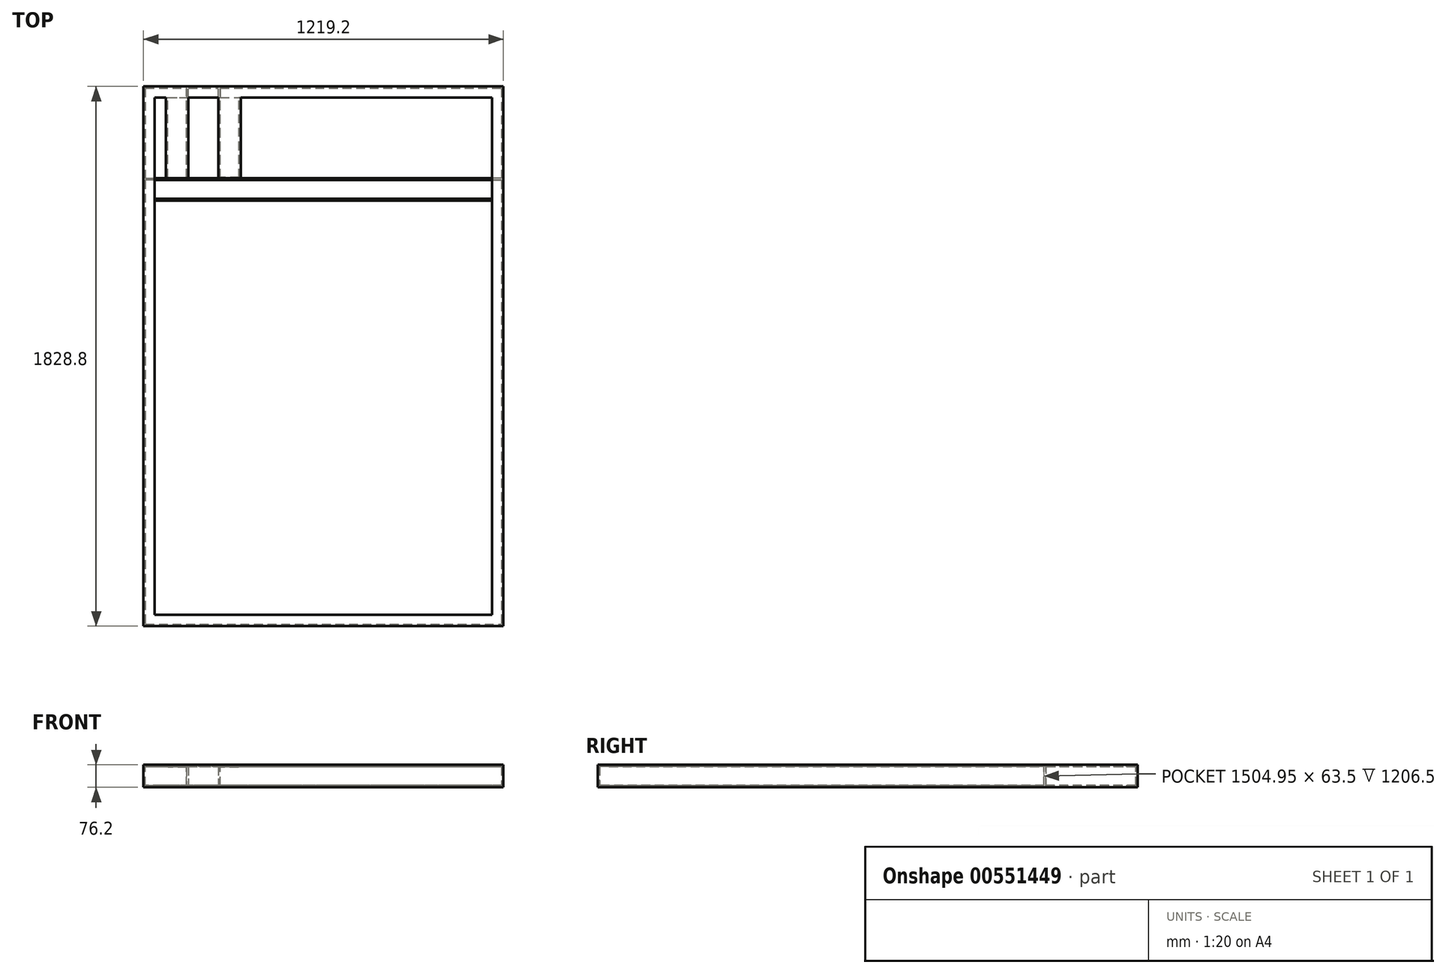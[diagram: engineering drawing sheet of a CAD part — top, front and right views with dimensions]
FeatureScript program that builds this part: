
annotation { "Feature Type Name" : "Feature", "Feature Type Description" : "" }
export const myFeature = defineFeature(function(context is Context, id is Id, definition is map)
    precondition{}
    {
        {
            var Q0;
            Q0=qCreatedBy(makeId("Top.planeOp"),FACE);
            var sketch = newSketch(context, id + "F0", { "sketchPlane" : qUnion([Q0])});
            skLineSegment(sketch, "E0.bottom", {"start": v(-609.6, 914.4) * mm, "end": v(609.6, 914.4) * mm});
            skLineSegment(sketch, "E0.top", {"start": v(-609.6, -914.4) * mm, "end": v(609.6, -914.4) * mm});
            skLineSegment(sketch, "E0.left", {"start": v(-609.6, 914.4) * mm, "end": v(-609.6, -914.4) * mm});
            skLineSegment(sketch, "E0.right", {"start": v(609.6, 914.4) * mm, "end": v(609.6, -914.4) * mm});
            skSolve(sketch);
        }
        {
            var Q0;
            Q0 = qSketchRegion(id + "F0", true);
            extrude(context, id + "F1", {"entities" : qUnion([Q0]), "depth" : 76.2 * mm, "offsetDistance" : 25.4 * mm});
        }
        {
            var Q0;
            Q0=makeQuery(id+"F1.opExtrude","CAP_FACE",FACE,{"disambiguationData":[OSD([sQuery(id+"F0.wireOp",EDGE,"E0.bottom"),sQuery(id+"F0.wireOp",EDGE,"E0.top"),sQuery(id+"F0.wireOp",EDGE,"E0.left"),sQuery(id+"F0.wireOp",EDGE,"E0.right")])],"isStart":false});
            var sketch = newSketch(context, id + "F2", { "sketchPlane" : qUnion([Q0])});
            skLineSegment(sketch, "E1.MirrorCS", {"start": v(-571.5, 876.3) * mm, "end": v(571.5, 876.3) * mm});
            skLineSegment(sketch, "E2.MirrorCS", {"start": v(-571.5, -876.3) * mm, "end": v(-571.5, 876.3) * mm});
            skLineSegment(sketch, "E3.MirrorCS", {"start": v(-571.5, -876.3) * mm, "end": v(571.5, -876.3) * mm});
            skLineSegment(sketch, "E4.MirrorCS", {"start": v(571.5, -876.3) * mm, "end": v(571.5, 876.3) * mm});
            skSolve(sketch);
        }
        {
            var Q0;
            Q0 = qSketchRegion(id + "F2", true);
            extrude(context, id + "F3", {"entities" : qUnion([Q0]), "operationType" : NewBodyOperationType.REMOVE, "endBound" : BoundingType.THROUGH_ALL, "oppositeDirection" : true, "depth" : 25.4 * mm, "offsetDistance" : 25.4 * mm});
        }
        {
            var Q0;
            Q0=makeQuery(id+"F3.boolean.opBoolean","COPY",FACE,{"derivedFrom":makeQuery(id+"F3.opExtrude","SWEPT_FACE",FACE,{"disambiguationData":[OSD([sQuery(id+"F2.wireOp",EDGE,"E2.MirrorCS")])]})});
            var Q1;
            Q1=makeQuery(id+"F3.boolean.opBoolean","COPY",FACE,{"derivedFrom":makeQuery(id+"F3.opExtrude","SWEPT_FACE",FACE,{"disambiguationData":[OSD([sQuery(id+"F2.wireOp",EDGE,"BSWPrCAb-DWeY-rpQ2-p5fh-YIavBrtnFnHP.left")])]})});
            var Q2;
            Q2=makeQuery(id+"F3.boolean.opBoolean","COPY",FACE,{"derivedFrom":makeQuery(id+"F3.opExtrude","SWEPT_FACE",FACE,{"disambiguationData":[OSD([sQuery(id+"F2.wireOp",EDGE,"BSWPrCAb-DWeY-rpQ2-p5fh-YIavBrtnFnHP.bottom")])]})});
            var Q3;
            Q3=makeQuery(id+"F3.boolean.opBoolean","COPY",FACE,{"derivedFrom":makeQuery(id+"F3.opExtrude","SWEPT_FACE",FACE,{"disambiguationData":[OSD([sQuery(id+"F2.wireOp",EDGE,"BSWPrCAb-DWeY-rpQ2-p5fh-YIavBrtnFnHP.right")])]})});
            var Q4;
            Q4=makeQuery(id+"F3.boolean.opBoolean","COPY",FACE,{"derivedFrom":makeQuery(id+"F3.opExtrude","SWEPT_FACE",FACE,{"disambiguationData":[OSD([sQuery(id+"F2.wireOp",EDGE,"E4.MirrorCS")])]})});
            var Q5;
            Q5=makeQuery(id+"F3.boolean.opBoolean","COPY",FACE,{"derivedFrom":makeQuery(id+"F3.opExtrude","SWEPT_FACE",FACE,{"disambiguationData":[OSD([sQuery(id+"F2.wireOp",EDGE,"E1.MirrorCS")])]})});
            var Q6;
            Q6=makeQuery(id+"F3.boolean.opBoolean","COPY",FACE,{"derivedFrom":makeQuery(id+"F3.opExtrude","SWEPT_FACE",FACE,{"disambiguationData":[OSD([sQuery(id+"F2.wireOp",EDGE,"E3.MirrorCS")])]})});
            shell(context, id + "F4", {"entities" : qUnion([Q0, Q1, Q2, Q3, Q4, Q5, Q6]), "thickness" : 6.35 * mm});
        }
        {
            var Q0;
            Q0=makeQuery(id+"F4.opShell","OFFSET_FACE",FACE,{"disambiguationData":[OSD([sQuery(id+"F0.wireOp",EDGE,"E0.left")])]});
            var sketch = newSketch(context, id + "F5", { "sketchPlane" : qUnion([Q0])});
            skLineSegment(sketch, "E5", {"start": v(527.05, 0) * mm, "end": v(603.25, 0) * mm});
            skLineSegment(sketch, "E6", {"start": v(603.25, 0) * mm, "end": v(603.25, 76.2) * mm});
            skLineSegment(sketch, "E7", {"start": v(603.25, 76.2) * mm, "end": v(527.05, 0) * mm});
            skSolve(sketch);
        }
        {
            var Q0;
            Q0 = qSketchRegion(id + "F5", true);
            extrude(context, id + "F6", {"entities" : qUnion([Q0]), "operationType" : NewBodyOperationType.ADD, "endBound" : BoundingType.UP_TO_NEXT, "depth" : 914.4 * mm, "offsetDistance" : 25.4 * mm});
        }
        {
            var Q0;
            Q0=makeQuery(id+"F6.opExtrude","SWEPT_FACE",FACE,{"disambiguationData":[OSD([sQuery(id+"F5.wireOp",EDGE,"E7")])]});
            shell(context, id + "F7", {"entities" : qUnion([Q0]), "thickness" : 6.35 * mm});
        }
        {
            var Q0;
            Q0=makeQuery(id+"F4.opShell","OFFSET_FACE",FACE,{"disambiguationData":[OSD([sQuery(id+"F0.wireOp",EDGE,"E0.bottom")])]});
            var sketch = newSketch(context, id + "F8", { "sketchPlane" : qUnion([Q0])});
            skLineSegment(sketch, "E8", {"start": v(-457.2, 76.2) * mm, "end": v(-457.2, 0) * mm});
            skLineSegment(sketch, "E9", {"start": v(-457.2, 0) * mm, "end": v(-533.4, 76.2) * mm});
            skLineSegment(sketch, "E10", {"start": v(-533.4, 76.2) * mm, "end": v(-457.2, 76.2) * mm});
            skLineSegment(sketch, "E11", {"start": v(-406.4, 105.97) * mm, "end": v(-406.4, 6.35) * mm, "construction": true});
            skLineSegment(sketch, "E12.MirrorCS", {"start": v(-355.6, 76.2) * mm, "end": v(-355.6, 0) * mm});
            skLineSegment(sketch, "E13.MirrorCS", {"start": v(-355.6, 0) * mm, "end": v(-279.4, 76.2) * mm});
            skLineSegment(sketch, "E14.MirrorCS", {"start": v(-279.4, 76.2) * mm, "end": v(-355.6, 76.2) * mm});
            skSolve(sketch);
        }
        {
            var Q0;
            {var subQ0=sQuery(id+"F8.wireOp",EDGE,"E9");var subQ1=sQuery(id+"F8.wireOp",EDGE,"E8");var subQ2=makeQuery(id+"F8.imprint","INTERSECT",VERTEX,{"derivedFrom":[subQ1,subQ0]});Q0=makeQuery(id+"F8.imprint","IMPRINT",FACE,{"disambiguationData":[TD([[makeQuery(id+"F8.imprint","IMPRINT",EDGE,{"disambiguationData":[TD([[subQ2,1.0]])],"derivedFrom":subQ1}),-1.0]])]});}
            var Q1;
            {var subQ0=sQuery(id+"F8.wireOp",EDGE,"E13.MirrorCS");var subQ1=sQuery(id+"F8.wireOp",EDGE,"E12.MirrorCS");var subQ2=makeQuery(id+"F8.imprint","INTERSECT",VERTEX,{"derivedFrom":[subQ1,subQ0]});Q1=makeQuery(id+"F8.imprint","IMPRINT",FACE,{"disambiguationData":[TD([[makeQuery(id+"F8.imprint","IMPRINT",EDGE,{"disambiguationData":[TD([[subQ2,1.0]])],"derivedFrom":subQ1}),1.0]])]});}
            var Q2;
            {var subQ0=sQuery(id+"F8.wireOp",EDGE,"E12.MirrorCS");var subQ1=sQuery(id+"F0.wireOp",EDGE,"E0.bottom");var subQ2=makeQuery(id+"F4.opShell","OFFSET_EDGE",EDGE,{"disambiguationData":[OSD([subQ1]),TDD([makeQuery(id+"F1.opExtrude","CAP_EDGE",EDGE,{"disambiguationData":[OSD([subQ1])],"isStart":false})])]});var subQ3=makeQuery(id+"F8.imprint","INTERSECT",VERTEX,{"derivedFrom":[subQ2,subQ0]});Q2=makeQuery(id+"F8.imprint","IMPRINT",FACE,{"disambiguationData":[TD([[makeQuery(id+"F8.imprint","IMPRINT",EDGE,{"disambiguationData":[TD([[subQ3,-1.0]])],"derivedFrom":subQ0}),1.0]])]});}
            var Q3;
            {var subQ0=sQuery(id+"F8.wireOp",EDGE,"E8");var subQ1=sQuery(id+"F0.wireOp",EDGE,"E0.bottom");var subQ2=makeQuery(id+"F4.opShell","OFFSET_EDGE",EDGE,{"disambiguationData":[OSD([subQ1]),TDD([makeQuery(id+"F1.opExtrude","CAP_EDGE",EDGE,{"disambiguationData":[OSD([subQ1])],"isStart":false})])]});var subQ3=makeQuery(id+"F8.imprint","INTERSECT",VERTEX,{"derivedFrom":[subQ2,subQ0]});Q3=makeQuery(id+"F8.imprint","IMPRINT",FACE,{"disambiguationData":[TD([[makeQuery(id+"F8.imprint","IMPRINT",EDGE,{"disambiguationData":[TD([[subQ3,-1.0]])],"derivedFrom":subQ0}),-1.0]])]});}
            var Q4;
            {var subQ0=sQuery(id+"F8.wireOp",EDGE,"E14.MirrorCS");Q4=makeQuery(id+"F8.imprint","IMPRINT",FACE,{"disambiguationData":[TD([[makeQuery(id+"F8.imprint","IMPRINT",EDGE,{"derivedFrom":subQ0}),1.0]])]});}
            var Q5;
            {var subQ0=sQuery(id+"F8.wireOp",EDGE,"E10");Q5=makeQuery(id+"F8.imprint","IMPRINT",FACE,{"disambiguationData":[TD([[makeQuery(id+"F8.imprint","IMPRINT",EDGE,{"derivedFrom":subQ0}),-1.0]])]});}
            extrude(context, id + "F9", {"entities" : qUnion([Q0, Q1, Q2, Q3, Q4, Q5]), "operationType" : NewBodyOperationType.ADD, "depth" : 304.8 * mm, "offsetDistance" : 25.4 * mm});
        }
        {
            var Q0;
            Q0=makeQuery(id+"F9.opExtrude","SWEPT_FACE",FACE,{"disambiguationData":[OSD([sQuery(id+"F8.wireOp",EDGE,"E9")])]});
            var Q1;
            Q1=makeQuery(id+"F9.opExtrude","SWEPT_FACE",FACE,{"disambiguationData":[OSD([sQuery(id+"F8.wireOp",EDGE,"E13.MirrorCS")])]});
            var Q2;
            Q2=makeQuery(id+"F9.opExtrude","CAP_FACE",FACE,{"disambiguationData":[OSD([sQuery(id+"F0.wireOp",EDGE,"E0.bottom"),sQuery(id+"F8.wireOp",EDGE,"E8"),sQuery(id+"F8.wireOp",EDGE,"E9")])],"isStart":false});
            var Q3;
            Q3=makeQuery(id+"F9.opExtrude","CAP_FACE",FACE,{"disambiguationData":[OSD([sQuery(id+"F0.wireOp",EDGE,"E0.bottom"),sQuery(id+"F8.wireOp",EDGE,"E12.MirrorCS"),sQuery(id+"F8.wireOp",EDGE,"E13.MirrorCS")])],"isStart":false});
            shell(context, id + "F10", {"entities" : qUnion([Q0, Q1, Q2, Q3]), "thickness" : 6.35 * mm});
        }
    });
